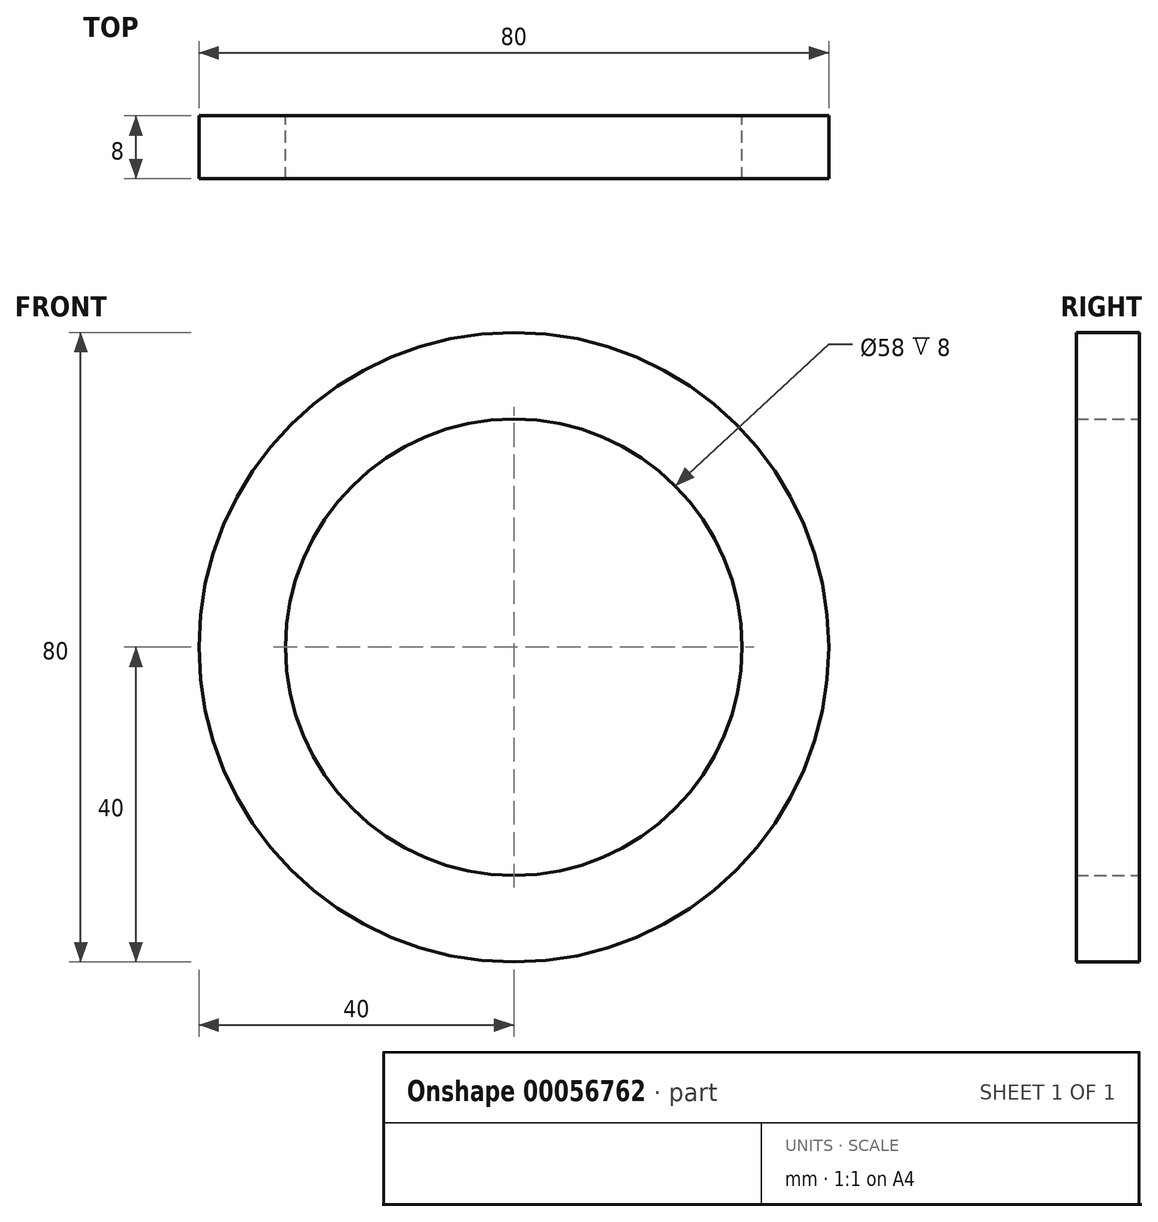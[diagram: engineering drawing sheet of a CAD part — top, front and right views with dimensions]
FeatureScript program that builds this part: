
annotation { "Feature Type Name" : "Feature", "Feature Type Description" : "" }
export const myFeature = defineFeature(function(context is Context, id is Id, definition is map)
    precondition{}
    {
        {
            var Q0;
            Q0=qCreatedBy(makeId("Front.planeOp"),FACE);
            var sketch = newSketch(context, id + "F0", { "sketchPlane" : qUnion([Q0])});
            skCircle(sketch, "E0", {"center": v(0, 0) * mm, "radius": 29 * mm});
            skCircle(sketch, "E1", {"center": v(0, 0) * mm, "radius": 40 * mm});
            skSolve(sketch);
        }
        {
            var Q0;
            Q0 = qSketchRegion(id + "F0", true);
            extrude(context, id + "F1", {"entities" : qUnion([Q0]), "depth" : 8 * mm});
        }
    });
